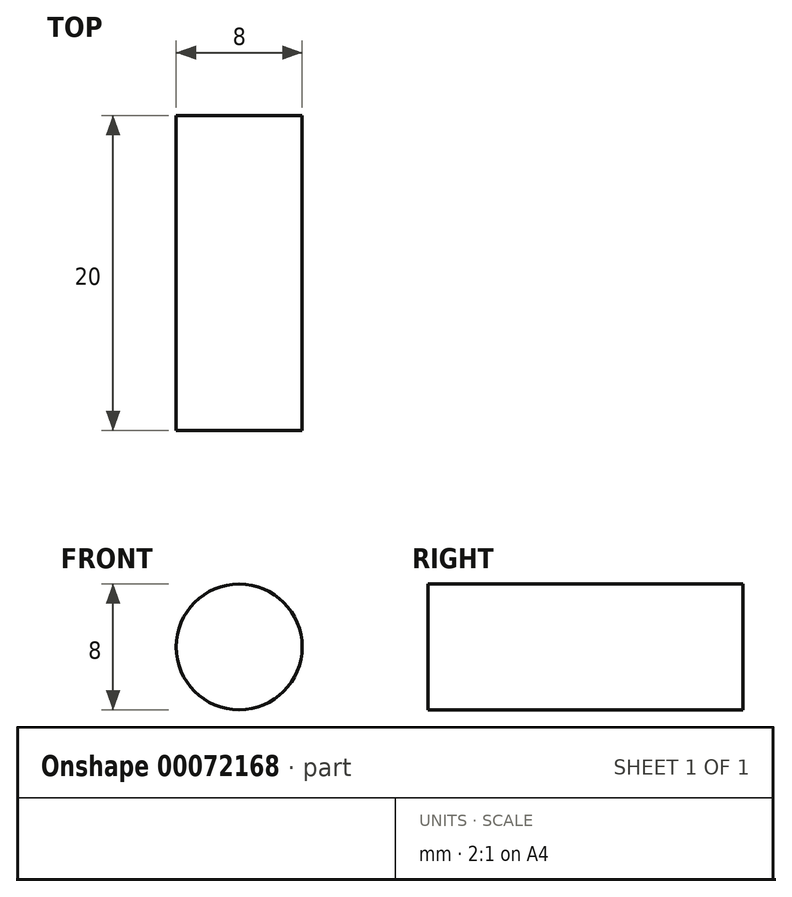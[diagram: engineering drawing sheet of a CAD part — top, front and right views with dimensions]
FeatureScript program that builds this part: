
annotation { "Feature Type Name" : "Feature", "Feature Type Description" : "" }
export const myFeature = defineFeature(function(context is Context, id is Id, definition is map)
    precondition{}
    {
        {
            var Q0;
            Q0=qCreatedBy(makeId("Front.planeOp"),FACE);
            var sketch = newSketch(context, id + "F0", { "sketchPlane" : qUnion([Q0])});
            skCircle(sketch, "E0", {"center": v(0, 0) * mm, "radius": 4 * mm});
            skSolve(sketch);
        }
        {
            var Q0;
            Q0 = qSketchRegion(id + "F0", true);
            extrude(context, id + "F1", {"entities" : qUnion([Q0]), "depth" : 20 * mm});
        }
    });
